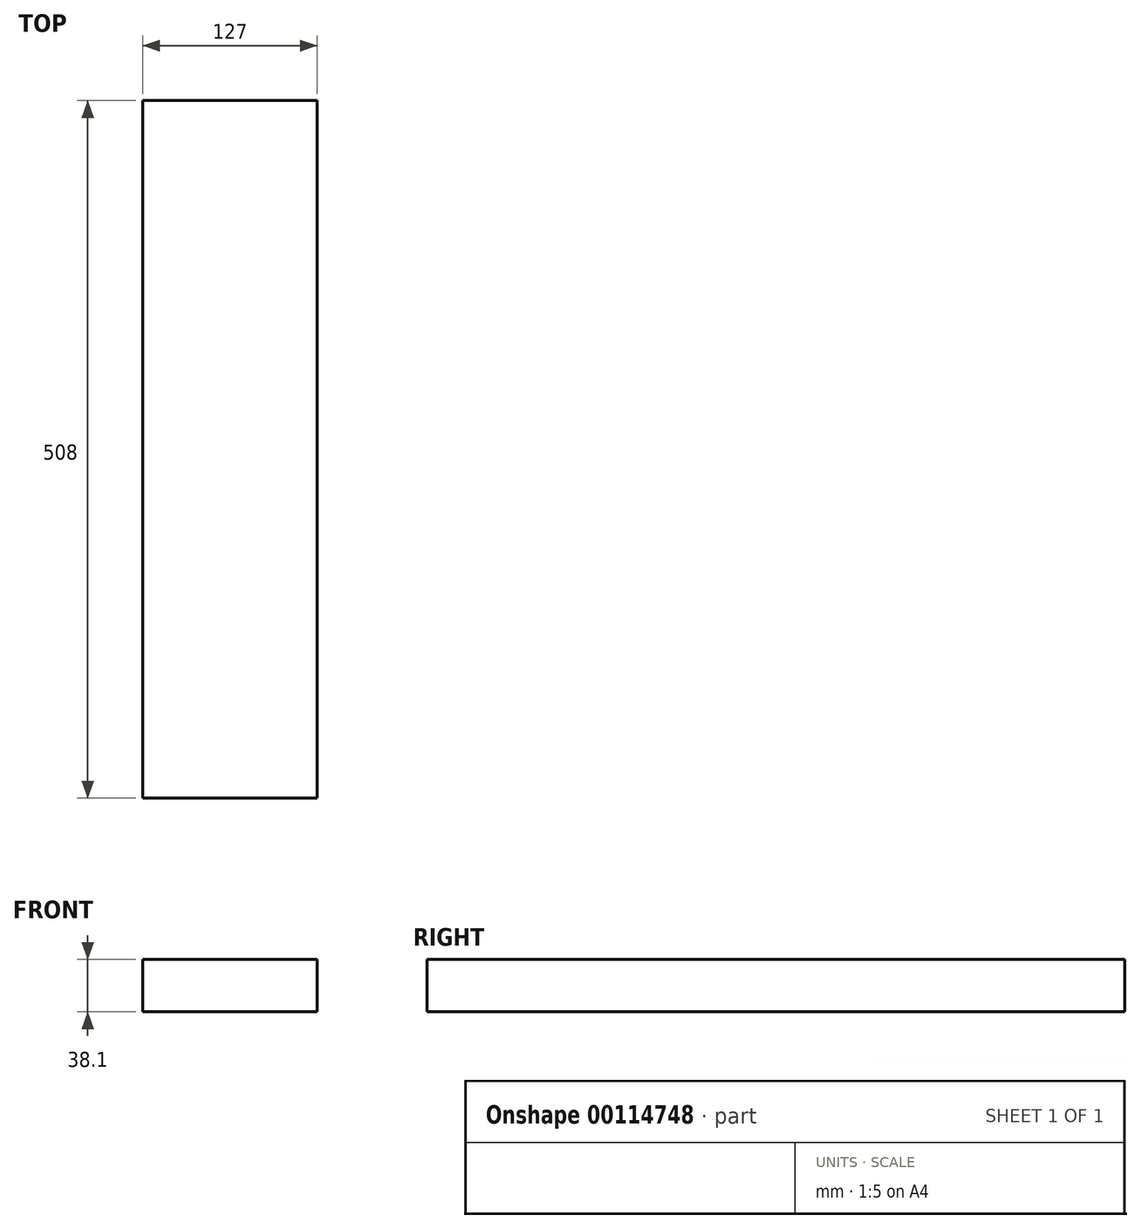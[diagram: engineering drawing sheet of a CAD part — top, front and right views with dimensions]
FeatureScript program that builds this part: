
annotation { "Feature Type Name" : "Feature", "Feature Type Description" : "" }
export const myFeature = defineFeature(function(context is Context, id is Id, definition is map)
    precondition{}
    {
        {
            var Q0;
            Q0=qCreatedBy(makeId("Top.planeOp"),FACE);
            var sketch = newSketch(context, id + "F0", { "sketchPlane" : qUnion([Q0])});
            skLineSegment(sketch, "E0.bottom", {"start": v(0, 0) * mm, "end": v(127, 0) * mm});
            skLineSegment(sketch, "E0.top", {"start": v(0, 508) * mm, "end": v(127, 508) * mm});
            skLineSegment(sketch, "E0.left", {"start": v(0, 0) * mm, "end": v(0, 508) * mm});
            skLineSegment(sketch, "E0.right", {"start": v(127, 0) * mm, "end": v(127, 508) * mm});
            skSolve(sketch);
        }
        {
            var Q0;
            Q0=qSketchRegion(id+"F0",true);
            extrude(context, id + "F1", {"entities" : qUnion([Q0]), "depth" : 38.1 * mm});
        }
    });
